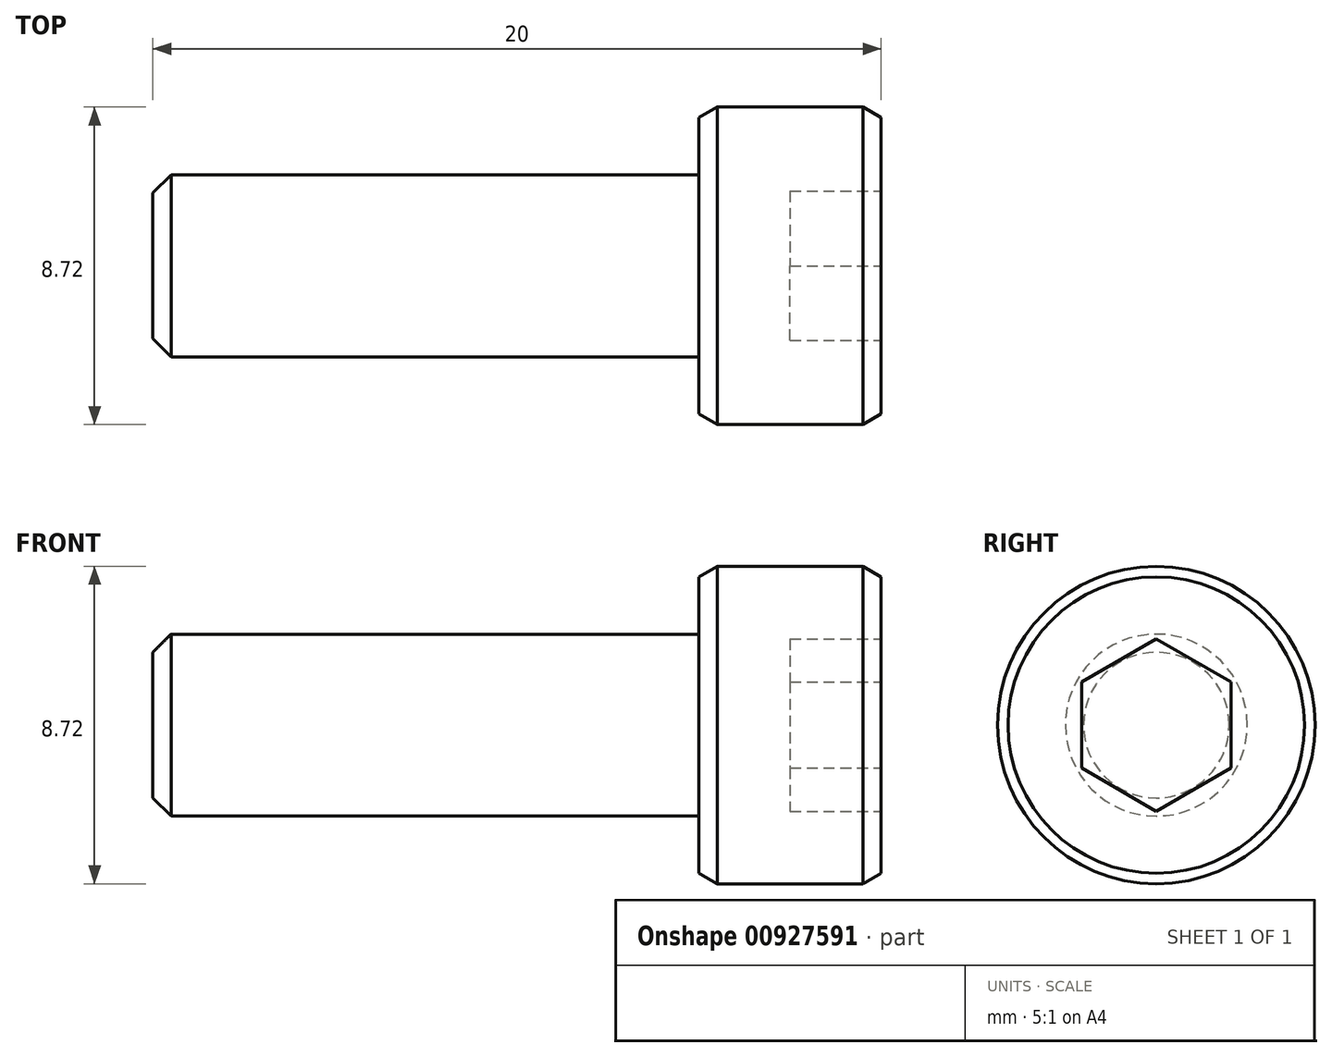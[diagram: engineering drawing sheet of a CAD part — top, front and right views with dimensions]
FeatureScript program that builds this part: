
annotation { "Feature Type Name" : "Feature", "Feature Type Description" : "" }
export const myFeature = defineFeature(function(context is Context, id is Id, definition is map)
    precondition{}
    {
        {
            var Q0;
            Q0=qCreatedBy(makeId("Right.planeOp"),FACE);
            var sketch = newSketch(context, id + "F0", { "sketchPlane" : qUnion([Q0])});
            skCircle(sketch, "E0", {"center": v(0, 0) * mm, "radius": 4.36 * mm});
            skSolve(sketch);
        }
        {
            var Q0;
            Q0 = qSketchRegion(id + "F0", true);
            extrude(context, id + "F1", {"entities" : qUnion([Q0]), "oppositeDirection" : true, "depth" : 5 * mm, "offsetDistance" : 25 * mm});
        }
        {
            var Q0;
            Q0=makeQuery(id+"F1.opExtrude","CAP_EDGE",EDGE,{"disambiguationData":[OSD([sQuery(id+"F0.wireOp",EDGE,"E0")])],"isStart":true});
            var Q1;
            Q1=makeQuery(id+"F1.opExtrude","CAP_EDGE",EDGE,{"disambiguationData":[OSD([sQuery(id+"F0.wireOp",EDGE,"E0")])],"isStart":false});
            chamfer(context, id + "F2", {"entities" : qUnion([Q0, Q1]), "chamferType" : ChamferType.OFFSET_ANGLE, "width" : 0.5 * mm, "oppositeDirection" : true, "angle" : 30 * degree, "tangentPropagation" : true});
        }
        {
            var Q0;
            Q0=makeQuery(id+"F1.opExtrude","CAP_FACE",FACE,{"disambiguationData":[OSD([sQuery(id+"F0.wireOp",EDGE,"E0")])],"isStart":true});
            var sketch = newSketch(context, id + "F3", { "sketchPlane" : qUnion([Q0])});
            skLineSegment(sketch, "E1", {"start": v(0, 10.95) * mm, "end": v(0, -10.24) * mm, "construction": true});
            skLineSegment(sketch, "E2", {"start": v(-11.3, 0) * mm, "end": v(13.13, 0) * mm, "construction": true});
            skCircle(sketch, "E3.cCircle", {"center": v(0, 0) * mm, "radius": 2.05 * mm, "construction": true});
            skLineSegment(sketch, "E3.0", {"start": v(2.05, -1.18) * mm, "end": v(0, -2.36) * mm});
            skLineSegment(sketch, "E3.1", {"start": v(0, -2.36) * mm, "end": v(-2.05, -1.18) * mm});
            skLineSegment(sketch, "E3.2", {"start": v(-2.05, -1.18) * mm, "end": v(-2.05, 1.18) * mm});
            skLineSegment(sketch, "E3.3", {"start": v(-2.05, 1.18) * mm, "end": v(0, 2.36) * mm});
            skLineSegment(sketch, "E3.4", {"start": v(0, 2.36) * mm, "end": v(2.05, 1.18) * mm});
            skLineSegment(sketch, "E3.5", {"start": v(2.05, 1.18) * mm, "end": v(2.05, -1.18) * mm});
            skPoint(sketch, "E3.0.midPoint", {"position": v(1.02, -1.77) * mm});
            skSolve(sketch);
        }
        {
            var Q0;
            Q0 = qSketchRegion(id + "F3", true);
            extrude(context, id + "F4", {"entities" : qUnion([Q0]), "operationType" : NewBodyOperationType.REMOVE, "oppositeDirection" : true, "depth" : 2.5 * mm, "offsetDistance" : 25 * mm});
        }
        {
            var Q0;
            Q0=makeQuery(id+"F1.opExtrude","CAP_FACE",FACE,{"disambiguationData":[OSD([sQuery(id+"F0.wireOp",EDGE,"E0")])],"isStart":false});
            var sketch = newSketch(context, id + "F5", { "sketchPlane" : qUnion([Q0])});
            skCircle(sketch, "E4", {"center": v(0, 0) * mm, "radius": 2.5 * mm});
            skSolve(sketch);
        }
        {
            var Q0;
            Q0 = qSketchRegion(id + "F5", true);
            extrude(context, id + "F6", {"entities" : qUnion([Q0]), "operationType" : NewBodyOperationType.ADD, "depth" : 15 * mm, "offsetDistance" : 25 * mm});
        }
        {
            var Q0;
            Q0=makeQuery(id+"F6.opExtrude","CAP_EDGE",EDGE,{"disambiguationData":[OSD([sQuery(id+"F5.wireOp",EDGE,"E4")])],"isStart":false});
            chamfer(context, id + "F7", {"entities" : qUnion([Q0]), "width" : 0.5 * mm, "tangentPropagation" : true});
        }
    });
